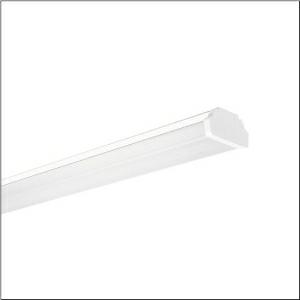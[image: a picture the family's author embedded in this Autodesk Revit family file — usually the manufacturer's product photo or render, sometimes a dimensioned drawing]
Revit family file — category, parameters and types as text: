
# Revit family: dus_r__31_mo_53bd81271v6080_96d5
name_source: partatom
category: Lighting Fixtures
units: mm (PartAtom-declared; Revit-internal decimal feet)

## family parameters
Cut with Voids When Loaded = No
Host = Face
Light Source = No
Part Type = Normal
Room Calculation Point = No
Round Connector Dimension = Use Diameter
Shared = No

## types (1)
- DUS® 31 MO (1 x LED, 7820 lm, 50.8 W, 6500K)
    Apparent Load = 51 VA
    CIE Flux Codes = 47 80 95 92 100
    Color Rendering = 80
    Color Temperature = 6500K
    Default Elevation = 1800 mm
    Description = DUS® 31 MOluminaire insert, length: 1.535mm, width: 81mm, height: 90mm, LED rated luminous flux: 7.820lm, light colour: 865, control gear: ON/OFF, control gear: ECG, with plug, 3-pole, with phase selection, mains connection: 220..240V, AC, 50/60Hz, primary optical cover: cover, of PMMA, light emission: direct distribution, primary light characteristic: symmetric, protection rating (complete): IP20, protection rating (LED compartment): IP50, insulation class (complete): insulation class I (protective earthing), certification: CE, ENEC, VDE, permissible ambient temperature for indoor applications: -35..+35°C, corresponds to IFS (International Featured Standards) requirements for safety and quality in the food industry, reducing of maximum allowable ambient temperature of 5°C with ceiling mounting, packaging unit: 1 piece
    Height = 95 mm
    Lamp = 1 x LED
    Lamp Light Flux = 7820 lm
    Lamp Power = 50.8 W
    Lamp count = 1
    Length = 1535 mm
    Luminous efficacy = 154 lm/W
    Manufacturer = Siteco
    ModVariant = No
    Model = 53BD81271V6080
    Mounting Place = Ceiling
    Mounting Type = Pendant
    Number of Poles = 1
    OnlyDefault = Yes
    Power Factor = 1
    Product Name = DUS® 31 MO
    Product group = luminaire insert
    ProductGroupID = 902
    Protection Class = Protection class I
    Protection Degree = IP 20
    RLX_Detail_Level = 1
    RlxData = <blob elided: 38385 chars, md5=618ca039>
    Socket = socket
    Standby Power = 0 W
    System Light Flux = 7820 lm
    System Power = 51 W
    Type Comments = Product without accessories
    Type Image = l_1003451.jpg
    URL = http://relux.com
    VarID = ---
    Voltage = 0 V
    Weight = 0.00 kg
    Width = 81 mm

## geometry (parser evidence)
native form markers: Blend x4, Sweep x12
no freeform markers — native parametric forms only
